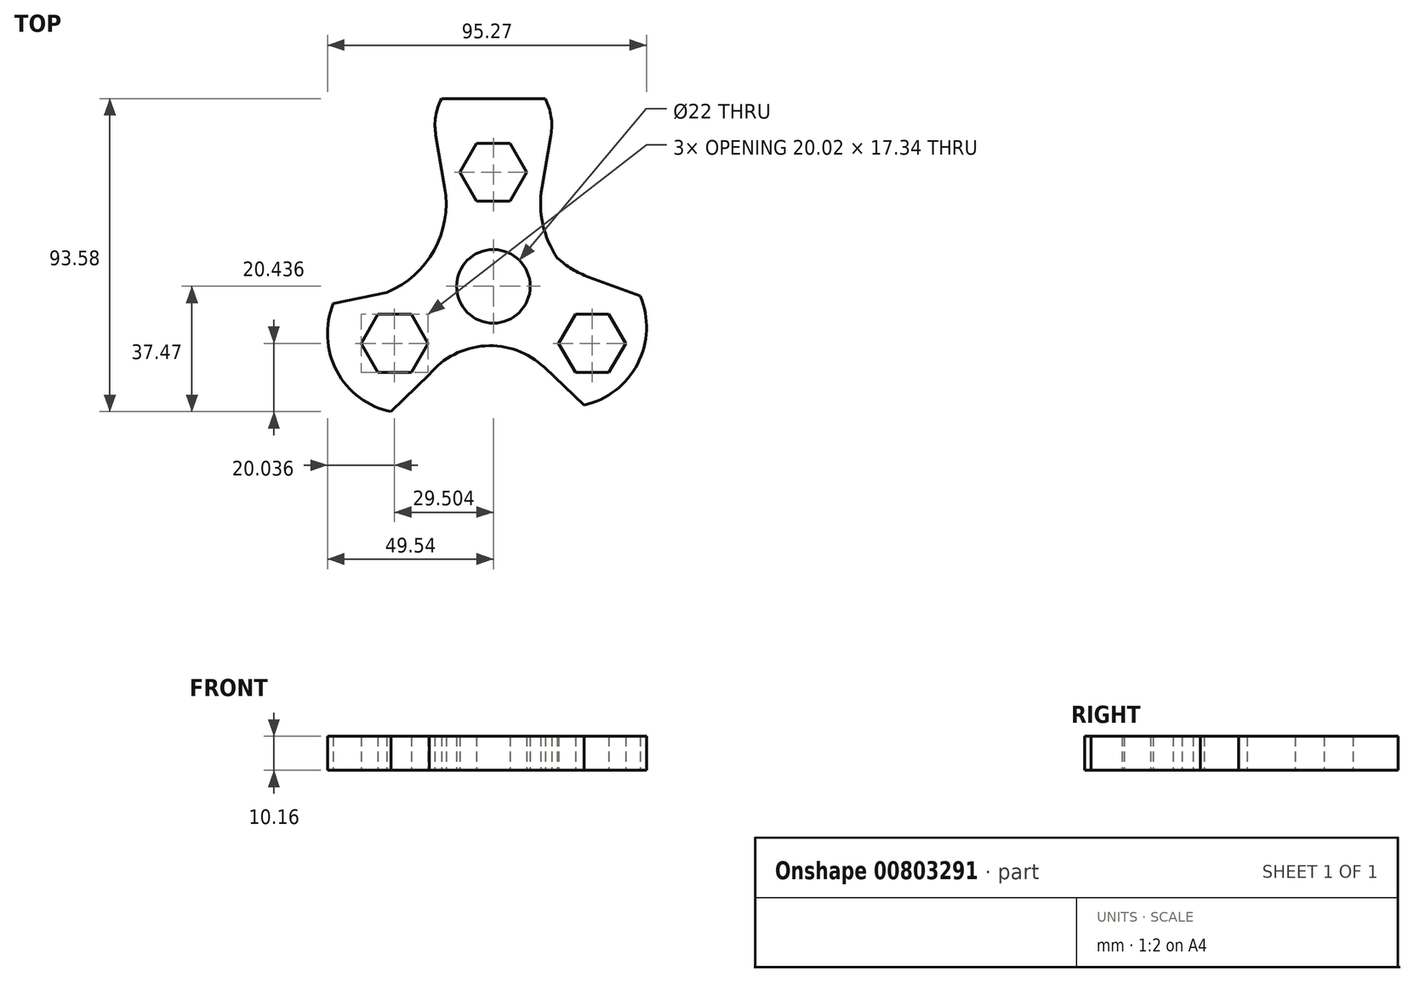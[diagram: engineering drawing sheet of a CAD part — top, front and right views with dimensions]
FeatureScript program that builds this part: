
annotation { "Feature Type Name" : "Feature", "Feature Type Description" : "" }
export const myFeature = defineFeature(function(context is Context, id is Id, definition is map)
    precondition{}
    {
        {
            var Q0;
            Q0=qCreatedBy(makeId("Top.planeOp"),FACE);
            var sketch = newSketch(context, id + "F0", { "sketchPlane" : qUnion([Q0])});
            skLineSegment(sketch, "E0", {"start": v(0, 0) * mm, "end": v(0, 25.4) * mm});
            skLineSegment(sketch, "E1", {"start": v(0, 25.4) * mm, "end": v(0, 34.07) * mm});
            skCircle(sketch, "E2.cCircle", {"center": v(0, 34.07) * mm, "radius": 8.67 * mm, "construction": true});
            skLineSegment(sketch, "E2.0", {"start": v(-5, 42.74) * mm, "end": v(5, 42.74) * mm});
            skLineSegment(sketch, "E2.1", {"start": v(5, 42.74) * mm, "end": v(10, 34.07) * mm});
            skLineSegment(sketch, "E2.2", {"start": v(10, 34.07) * mm, "end": v(5, 25.4) * mm});
            skLineSegment(sketch, "E2.3", {"start": v(5, 25.4) * mm, "end": v(-5, 25.4) * mm});
            skLineSegment(sketch, "E2.4", {"start": v(-5, 25.4) * mm, "end": v(-10, 34.07) * mm});
            skLineSegment(sketch, "E2.5", {"start": v(-10, 34.07) * mm, "end": v(-5, 42.74) * mm});
            skPoint(sketch, "E2.0.midPoint", {"position": v(0, 42.74) * mm});
            skLineSegment(sketch, "E3", {"start": v(-11.73, 81.5) * mm, "end": v(0.97, 81.5) * mm});
            skLineSegment(sketch, "E4", {"start": v(0, 0) * mm, "end": v(-22, -12.7) * mm});
            skLineSegment(sketch, "E5", {"start": v(0, 0) * mm, "end": v(22, -12.7) * mm});
            skLineSegment(sketch, "E6", {"start": v(-22, -12.7) * mm, "end": v(-29.5, -17.03) * mm});
            skCircle(sketch, "E7.cCircle", {"center": v(-29.5, -17.03) * mm, "radius": 8.67 * mm, "construction": true});
            skLineSegment(sketch, "E7.0", {"start": v(-24.5, -8.37) * mm, "end": v(-19.5, -17.03) * mm});
            skLineSegment(sketch, "E7.1", {"start": v(-19.5, -17.03) * mm, "end": v(-24.5, -25.7) * mm});
            skLineSegment(sketch, "E7.2", {"start": v(-24.5, -25.7) * mm, "end": v(-34.5, -25.7) * mm});
            skLineSegment(sketch, "E7.3", {"start": v(-34.5, -25.7) * mm, "end": v(-39.51, -17.03) * mm});
            skLineSegment(sketch, "E7.4", {"start": v(-39.51, -17.03) * mm, "end": v(-34.5, -8.37) * mm});
            skLineSegment(sketch, "E7.5", {"start": v(-34.5, -8.37) * mm, "end": v(-24.5, -8.37) * mm});
            skPoint(sketch, "E7.0.midPoint", {"position": v(-22, -12.7) * mm});
            skPoint(sketch, "E8.0.midPoint", {"position": v(22, -12.7) * mm});
            skLineSegment(sketch, "E9", {"start": v(0, 0) * mm, "end": v(0, 11) * mm});
            skLineSegment(sketch, "E10", {"start": v(0, 0) * mm, "end": v(0, -11) * mm});
            skCircle(sketch, "E11", {"center": v(0, 0) * mm, "radius": 11 * mm});
            skLineSegment(sketch, "E12", {"start": v(22, -12.7) * mm, "end": v(29.5, -17.03) * mm});
            skCircle(sketch, "E13.cCircle", {"center": v(29.5, -17.03) * mm, "radius": 8.66 * mm, "construction": true});
            skLineSegment(sketch, "E13.0", {"start": v(39.5, -17.03) * mm, "end": v(34.5, -25.7) * mm});
            skLineSegment(sketch, "E13.1", {"start": v(34.5, -25.7) * mm, "end": v(24.5, -25.7) * mm});
            skLineSegment(sketch, "E13.2", {"start": v(24.5, -25.7) * mm, "end": v(19.5, -17.03) * mm});
            skLineSegment(sketch, "E13.3", {"start": v(19.5, -17.03) * mm, "end": v(24.5, -8.37) * mm});
            skLineSegment(sketch, "E13.4", {"start": v(24.5, -8.37) * mm, "end": v(34.5, -8.37) * mm});
            skLineSegment(sketch, "E13.5", {"start": v(34.5, -8.37) * mm, "end": v(39.5, -17.03) * mm});
            skPoint(sketch, "E13.0.midPoint", {"position": v(37, -21.36) * mm});
            skArc(sketch, "E14.1.0", {"start": v(-47.78, -5.12) * mm, "mid": v(-46.74, -25.34) * mm, "end": v(-30.53, -37.47) * mm});
            skArc(sketch, "E14.2.0", {"start": v(27.07, -35.51) * mm, "mid": v(43.1, -23.14) * mm, "end": v(43.83, -2.92) * mm});
            skLineSegment(sketch, "E14.2.7", {"start": v(39.51, -17.03) * mm, "end": v(34.5, -25.7) * mm});
            skLineSegment(sketch, "E14.2.8", {"start": v(34.5, -8.37) * mm, "end": v(39.51, -17.03) * mm});
            skLineSegment(sketch, "E15", {"start": v(-47.78, -5.12) * mm, "end": v(-31.77, -1.8) * mm});
            skLineSegment(sketch, "E16", {"start": v(-30.53, -37.47) * mm, "end": v(-19.19, -26.35) * mm});
            skLineSegment(sketch, "E17", {"start": v(15.22, -24.24) * mm, "end": v(27.07, -35.51) * mm});
            skLineSegment(sketch, "E18", {"start": v(28.5, 2.76) * mm, "end": v(43.83, -2.92) * mm});
            skLineSegment(sketch, "E19", {"start": v(-14.5, 29.52) * mm, "end": v(-17.18, 45.18) * mm});
            skArc(sketch, "E20", {"start": v(19.13, 8.46) * mm, "mid": v(23.54, 5.16) * mm, "end": v(28.5, 2.76) * mm});
            skArc(sketch, "E21", {"start": v(-31.77, -1.8) * mm, "mid": v(-17.66, 10.84) * mm, "end": v(-14.5, 29.52) * mm});
            skArc(sketch, "E22", {"start": v(15.22, -24.24) * mm, "mid": v(-2.44, -17.8) * mm, "end": v(-19.19, -26.35) * mm});
            skLineSegment(sketch, "E23", {"start": v(-30.53, -37.47) * mm, "end": v(-47.78, -5.12) * mm});
            skLineSegment(sketch, "E24", {"start": v(-47.78, -5.12) * mm, "end": v(-30.53, -37.47) * mm});
            skArc(sketch, "E25.MirrorCS", {"start": v(19.13, 8.46) * mm, "mid": v(14.77, 18.54) * mm, "end": v(14.5, 29.52) * mm});
            skLineSegment(sketch, "E26.MirrorCS", {"start": v(14.5, 29.52) * mm, "end": v(17.18, 45.18) * mm});
            skPoint(sketch, "E27.orphan", {"position": v(31.77, -1.8) * mm});
            skPoint(sketch, "E28.MirrorCS.start.orphan", {"position": v(47.78, -5.12) * mm});
            skArc(sketch, "E29", {"start": v(17.18, 45.18) * mm, "mid": v(0, 65.54) * mm, "end": v(-17.18, 45.18) * mm});
            skLineSegment(sketch, "E30", {"start": v(-15.48, 56.11) * mm, "end": v(15.48, 56.11) * mm});
            skSolve(sketch);
        }
        {
            var Q0;
            Q0=makeQuery(id+"F0.imprint","IMPRINT",FACE,{"disambiguationData":[TD([[makeQuery(id+"F0.imprint","IMPRINT",EDGE,{"derivedFrom":sQuery(id+"F0.wireOp",EDGE,"E2.0")}),1.0]])]});
            extrude(context, id + "F1", {"entities" : qUnion([Q0]), "depth" : 10.16 * mm, "offsetDistance" : 25.4 * mm});
        }
        {
            var Q0;
            Q0=makeQuery(id+"F0.imprint","IMPRINT",FACE,{"disambiguationData":[TD([[makeQuery(id+"F0.imprint","IMPRINT",EDGE,{"derivedFrom":sQuery(id+"F0.wireOp",EDGE,"E14.1.0")}),1.0]])]});
            extrude(context, id + "F2", {"entities" : qUnion([Q0]), "operationType" : NewBodyOperationType.ADD, "depth" : 10.16 * mm, "offsetDistance" : 25.4 * mm});
        }
    });
